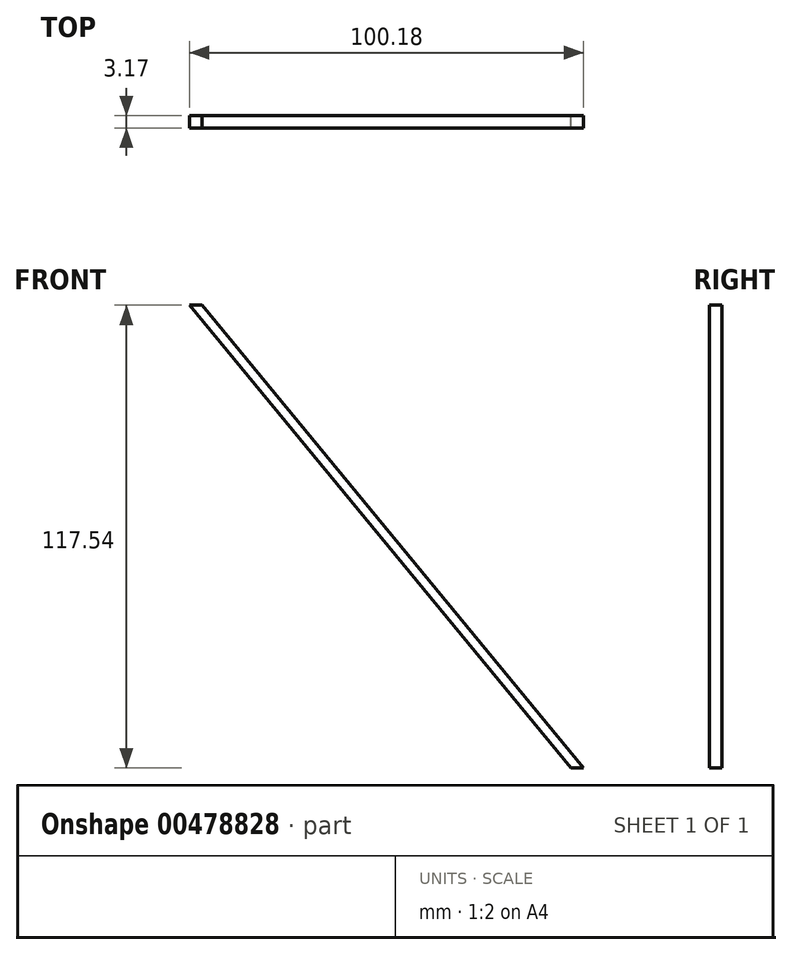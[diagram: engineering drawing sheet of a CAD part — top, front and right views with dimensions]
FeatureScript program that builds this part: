
annotation { "Feature Type Name" : "Feature", "Feature Type Description" : "" }
export const myFeature = defineFeature(function(context is Context, id is Id, definition is map)
    precondition{}
    {
        {
            var Q0;
            Q0=qCreatedBy(makeId("Front.planeOp"),FACE);
            var sketch = newSketch(context, id + "F0", { "sketchPlane" : qUnion([Q0])});
            skLineSegment(sketch, "E0", {"start": v(0, 117.54) * mm, "end": v(97, 0) * mm});
            skLineSegment(sketch, "E1", {"start": v(97, 0) * mm, "end": v(100.18, 0) * mm});
            skLineSegment(sketch, "E2", {"start": v(100.18, 0) * mm, "end": v(3.17, 117.54) * mm});
            skLineSegment(sketch, "E3", {"start": v(3.17, 117.54) * mm, "end": v(0, 117.54) * mm});
            skSolve(sketch);
        }
        {
            var Q0;
            Q0=makeQuery(id+"F0.imprint","IMPRINT",FACE,{"disambiguationData":[TD([[makeQuery(id+"F0.imprint","IMPRINT",EDGE,{"derivedFrom":sQuery(id+"F0.wireOp",EDGE,"E0")}),1.0]])]});
            extrude(context, id + "F1", {"entities" : qUnion([Q0]), "depth" : 3.17 * mm});
        }
    });
